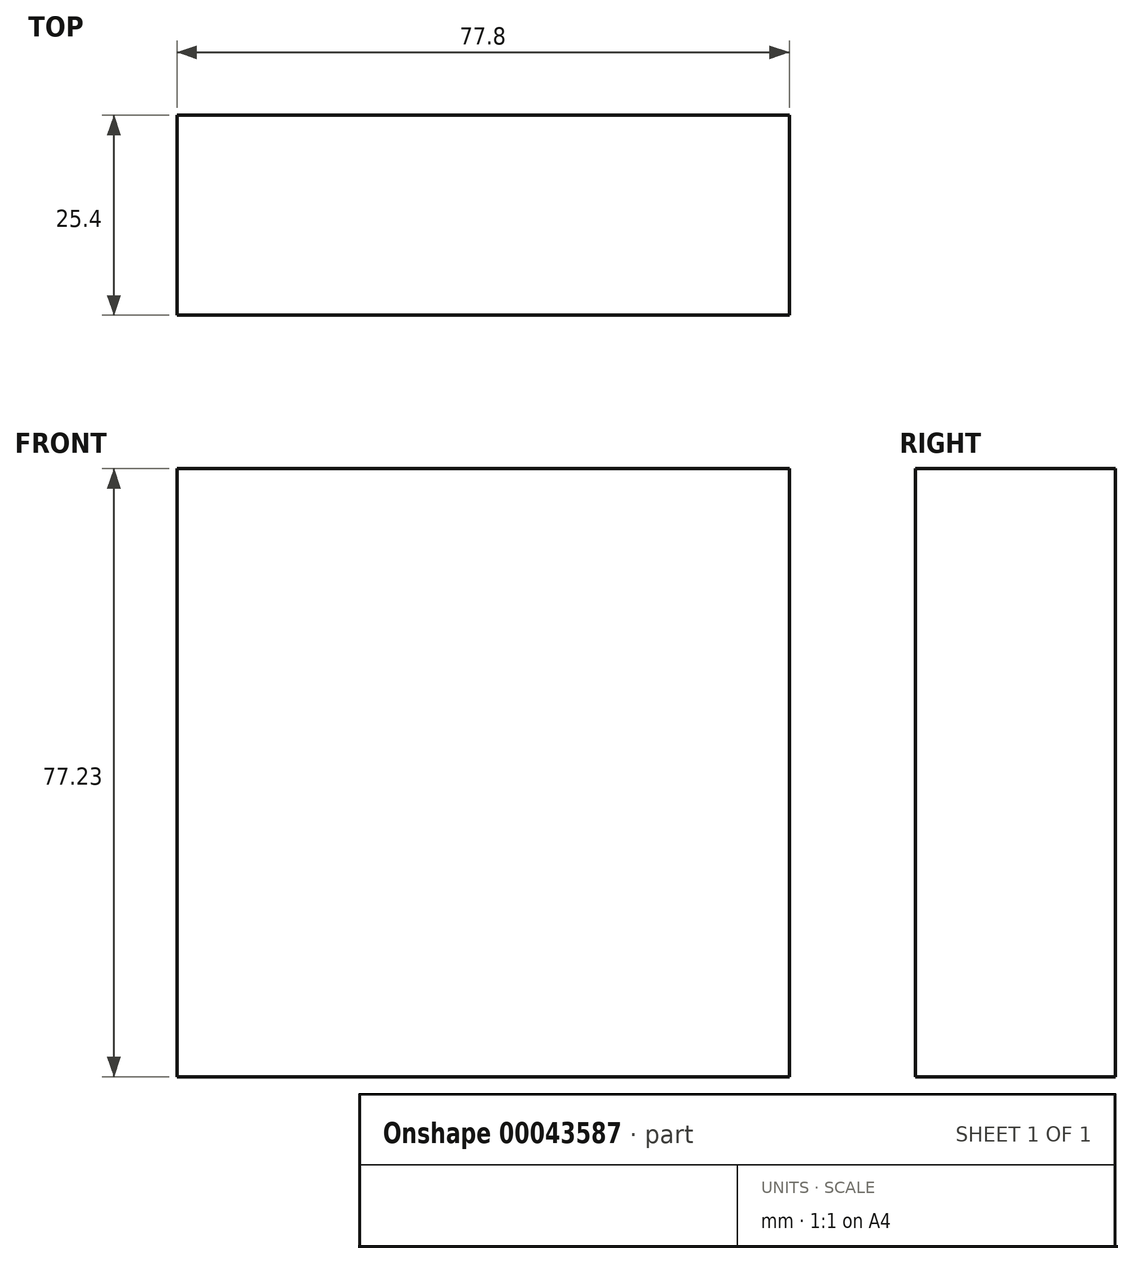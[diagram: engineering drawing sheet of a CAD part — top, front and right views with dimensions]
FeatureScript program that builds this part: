
annotation { "Feature Type Name" : "Feature", "Feature Type Description" : "" }
export const myFeature = defineFeature(function(context is Context, id is Id, definition is map)
    precondition{}
    {
        {
            var Q0;
            Q0=qCreatedBy(makeId("Front.planeOp"),FACE);
            var sketch = newSketch(context, id + "F0", { "sketchPlane" : qUnion([Q0])});
            skLineSegment(sketch, "E0.bottom", {"start": v(-38.62, 47.84) * mm, "end": v(39.18, 47.84) * mm});
            skLineSegment(sketch, "E0.top", {"start": v(-38.62, -29.39) * mm, "end": v(39.18, -29.39) * mm});
            skLineSegment(sketch, "E0.left", {"start": v(-38.62, 47.84) * mm, "end": v(-38.62, -29.39) * mm});
            skLineSegment(sketch, "E0.right", {"start": v(39.18, 47.84) * mm, "end": v(39.18, -29.39) * mm});
            skSolve(sketch);
        }
        {
            var Q0;
            Q0 = qSketchRegion(id + "F0", true);
            extrude(context, id + "F1", {"entities" : qUnion([Q0]), "depth" : 25.4 * mm});
        }
    });
